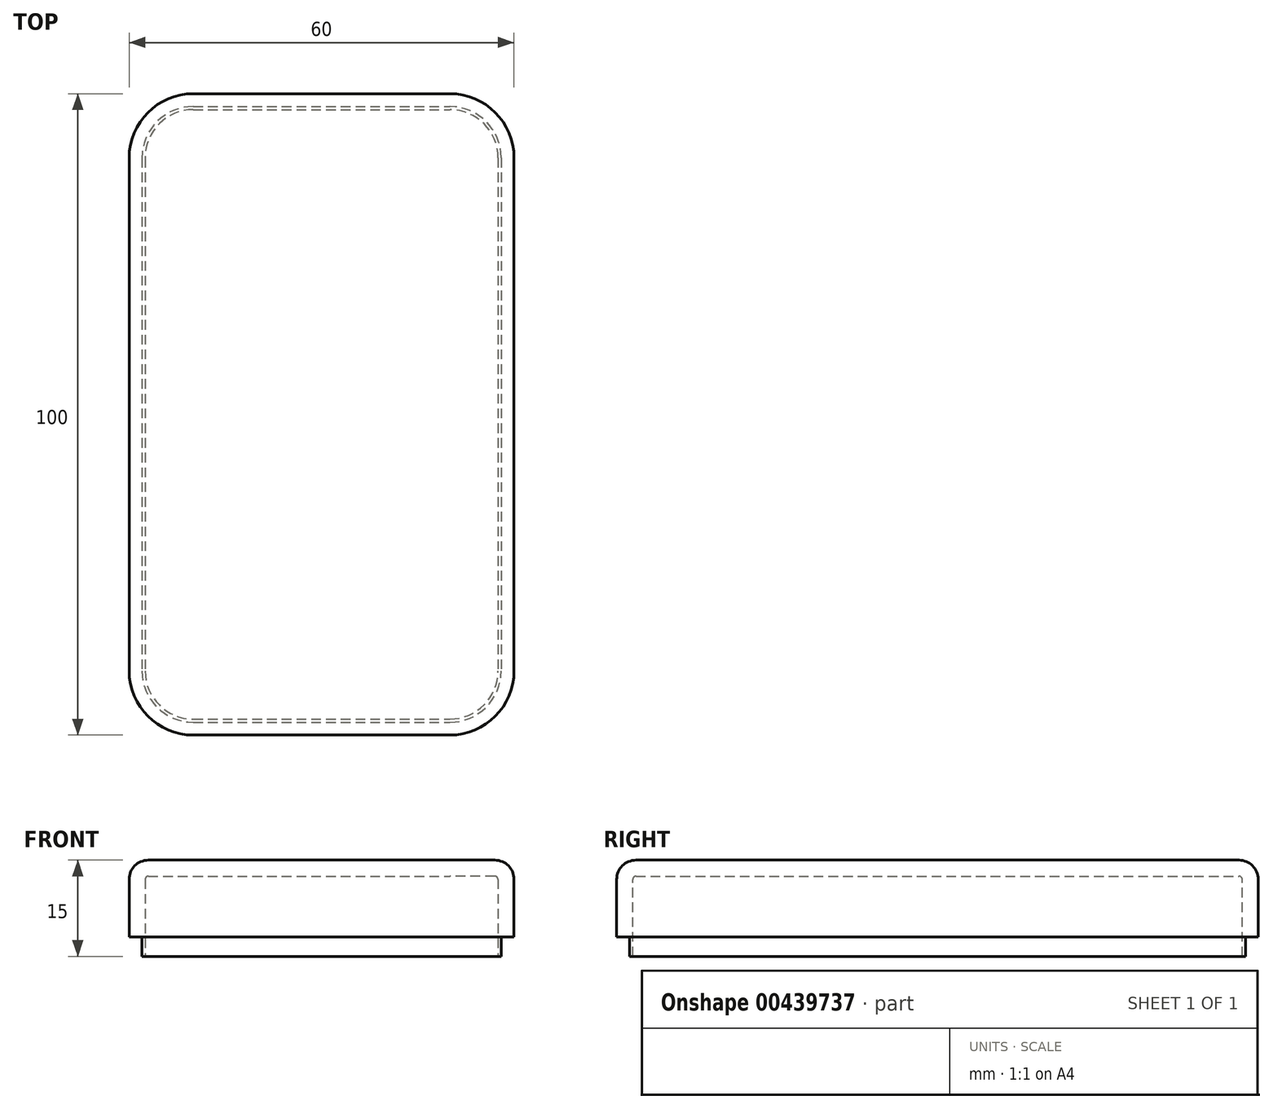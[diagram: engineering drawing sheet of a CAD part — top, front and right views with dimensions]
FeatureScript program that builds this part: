
annotation { "Feature Type Name" : "Feature", "Feature Type Description" : "" }
export const myFeature = defineFeature(function(context is Context, id is Id, definition is map)
    precondition{}
    {
        {
            var Q0;
            Q0=qCreatedBy(makeId("Top.planeOp"),FACE);
            var sketch = newSketch(context, id + "F0", { "sketchPlane" : qUnion([Q0])});
            skLineSegment(sketch, "E0.bottom", {"start": v(-29.68, 51.98) * mm, "end": v(30.32, 51.98) * mm});
            skLineSegment(sketch, "E0.top", {"start": v(-29.68, -48.02) * mm, "end": v(30.32, -48.02) * mm});
            skLineSegment(sketch, "E0.left", {"start": v(-29.68, 51.98) * mm, "end": v(-29.68, -48.02) * mm});
            skLineSegment(sketch, "E0.right", {"start": v(30.32, 51.98) * mm, "end": v(30.32, -48.02) * mm});
            skSolve(sketch);
        }
        {
            var Q0;
            Q0=makeQuery(id+"F0.imprint","IMPRINT",FACE,{"disambiguationData":[TD([[makeQuery(id+"F0.imprint","IMPRINT",EDGE,{"derivedFrom":sQuery(id+"F0.wireOp",EDGE,"E0.bottom")}),-1.0]])]});
            extrude(context, id + "F1", {"entities" : qUnion([Q0]), "depth" : 12 * mm});
        }
        {
            var Q0;
            Q0=makeQuery(id+"F1.opExtrude","SWEPT_EDGE",EDGE,{"disambiguationData":[OSD([sQuery(id+"F0.wireOp",EDGE,"E0.top"),sQuery(id+"F0.wireOp",EDGE,"E0.left")])]});
            var Q1;
            Q1=makeQuery(id+"F1.opExtrude","SWEPT_EDGE",EDGE,{"disambiguationData":[OSD([sQuery(id+"F0.wireOp",EDGE,"E0.bottom"),sQuery(id+"F0.wireOp",EDGE,"E0.left")])]});
            var Q2;
            Q2=makeQuery(id+"F1.opExtrude","SWEPT_EDGE",EDGE,{"disambiguationData":[OSD([sQuery(id+"F0.wireOp",EDGE,"E0.top"),sQuery(id+"F0.wireOp",EDGE,"E0.right")])]});
            var Q3;
            Q3=makeQuery(id+"F1.opExtrude","SWEPT_EDGE",EDGE,{"disambiguationData":[OSD([sQuery(id+"F0.wireOp",EDGE,"E0.bottom"),sQuery(id+"F0.wireOp",EDGE,"E0.right")])]});
            fillet(context, id + "F2", {"entities" : qUnion([Q0, Q1, Q2, Q3]), "radius" : 10 * mm, "tangentPropagation" : true, "allowEdgeOverflow" : false});
        }
        {
            var Q0;
            Q0=makeQuery(id+"F1.opExtrude","CAP_EDGE",EDGE,{"disambiguationData":[OSD([sQuery(id+"F0.wireOp",EDGE,"E0.bottom")])],"isStart":false});
            fillet(context, id + "F3", {"entities" : qUnion([Q0]), "radius" : 3 * mm, "tangentPropagation" : true, "allowEdgeOverflow" : false});
        }
        {
            var Q0;
            Q0=makeQuery(id+"F1.opExtrude","CAP_FACE",FACE,{"disambiguationData":[OSD([sQuery(id+"F0.wireOp",EDGE,"E0.bottom"),sQuery(id+"F0.wireOp",EDGE,"E0.top"),sQuery(id+"F0.wireOp",EDGE,"E0.left"),sQuery(id+"F0.wireOp",EDGE,"E0.right")])],"isStart":true});
            shell(context, id + "F4", {"entities" : qUnion([Q0]), "thickness" : 2.5 * mm});
        }
        {
            var Q0;
            Q0=makeQuery(id+"F1.opExtrude","CAP_FACE",FACE,{"disambiguationData":[OSD([sQuery(id+"F0.wireOp",EDGE,"E0.bottom"),sQuery(id+"F0.wireOp",EDGE,"E0.top"),sQuery(id+"F0.wireOp",EDGE,"E0.left"),sQuery(id+"F0.wireOp",EDGE,"E0.right")])],"isStart":true});
            var sketch = newSketch(context, id + "F5", { "sketchPlane" : qUnion([Q0])});
            skLineSegment(sketch, "E1.0", {"start": v(-27.18, -41.98) * mm, "end": v(-27.18, 38.02) * mm});
            skArc(sketch, "E2.0", {"start": v(-19.68, 45.52) * mm, "mid": v(-24.98, 43.33) * mm, "end": v(-27.18, 38.02) * mm});
            skLineSegment(sketch, "E3.0", {"start": v(-19.68, 45.52) * mm, "end": v(20.32, 45.52) * mm});
            skArc(sketch, "E4.0", {"start": v(27.82, 38.02) * mm, "mid": v(25.63, 43.33) * mm, "end": v(20.32, 45.52) * mm});
            skLineSegment(sketch, "E5.0", {"start": v(27.82, -41.98) * mm, "end": v(27.82, 38.02) * mm});
            skArc(sketch, "E6.0", {"start": v(20.32, -49.48) * mm, "mid": v(25.63, -47.28) * mm, "end": v(27.82, -41.98) * mm});
            skLineSegment(sketch, "E7.0", {"start": v(-19.68, -49.48) * mm, "end": v(20.32, -49.48) * mm});
            skPoint(sketch, "E8.0", {"position": v(-24.98, -47.28) * mm});
            skArc(sketch, "E9.0", {"start": v(-27.18, -41.98) * mm, "mid": v(-24.98, -47.28) * mm, "end": v(-19.68, -49.48) * mm});
            skArc(sketch, "E10.0", {"start": v(-27.68, -41.98) * mm, "mid": v(-25.33, -47.63) * mm, "end": v(-19.68, -49.98) * mm});
            skLineSegment(sketch, "E10.1", {"start": v(-19.68, -49.98) * mm, "end": v(20.32, -49.98) * mm});
            skLineSegment(sketch, "E10.2", {"start": v(-27.68, -41.98) * mm, "end": v(-27.68, 38.02) * mm});
            skArc(sketch, "E10.3", {"start": v(20.32, -49.98) * mm, "mid": v(25.98, -47.63) * mm, "end": v(28.32, -41.98) * mm});
            skArc(sketch, "E10.4", {"start": v(-19.68, 46.02) * mm, "mid": v(-25.33, 43.68) * mm, "end": v(-27.68, 38.02) * mm});
            skLineSegment(sketch, "E10.5", {"start": v(-19.68, 46.02) * mm, "end": v(20.32, 46.02) * mm});
            skArc(sketch, "E10.6", {"start": v(28.32, 38.02) * mm, "mid": v(25.98, 43.68) * mm, "end": v(20.32, 46.02) * mm});
            skLineSegment(sketch, "E10.7", {"start": v(28.32, -41.98) * mm, "end": v(28.32, 38.02) * mm});
            skArc(sketch, "E11.0", {"start": v(25.32, 38.02) * mm, "mid": v(23.86, 41.56) * mm, "end": v(20.32, 43.02) * mm});
            skLineSegment(sketch, "E11.1", {"start": v(25.32, -41.98) * mm, "end": v(25.32, 38.02) * mm});
            skLineSegment(sketch, "E11.2", {"start": v(20.32, 43.02) * mm, "end": v(-19.68, 43.02) * mm});
            skArc(sketch, "E11.3", {"start": v(20.32, -46.98) * mm, "mid": v(23.86, -45.51) * mm, "end": v(25.32, -41.98) * mm});
            skArc(sketch, "E11.4", {"start": v(-19.68, 43.02) * mm, "mid": v(-23.21, 41.56) * mm, "end": v(-24.68, 38.02) * mm});
            skLineSegment(sketch, "E11.5", {"start": v(-24.68, 38.02) * mm, "end": v(-24.68, -41.98) * mm});
            skArc(sketch, "E11.6", {"start": v(-24.68, -41.98) * mm, "mid": v(-23.21, -45.51) * mm, "end": v(-19.68, -46.98) * mm});
            skLineSegment(sketch, "E11.7", {"start": v(-19.68, -46.98) * mm, "end": v(20.32, -46.98) * mm});
            skSolve(sketch);
        }
        {
            var Q0;
            Q0=makeQuery(id+"F5.imprint","IMPRINT",FACE,{"disambiguationData":[TD([[makeQuery(id+"F5.imprint","IMPRINT",EDGE,{"derivedFrom":sQuery(id+"F5.wireOp",EDGE,"E1.0")}),1.0]])]});
            extrude(context, id + "F6", {"entities" : qUnion([Q0]), "operationType" : NewBodyOperationType.ADD, "depth" : 3 * mm});
        }
    });
